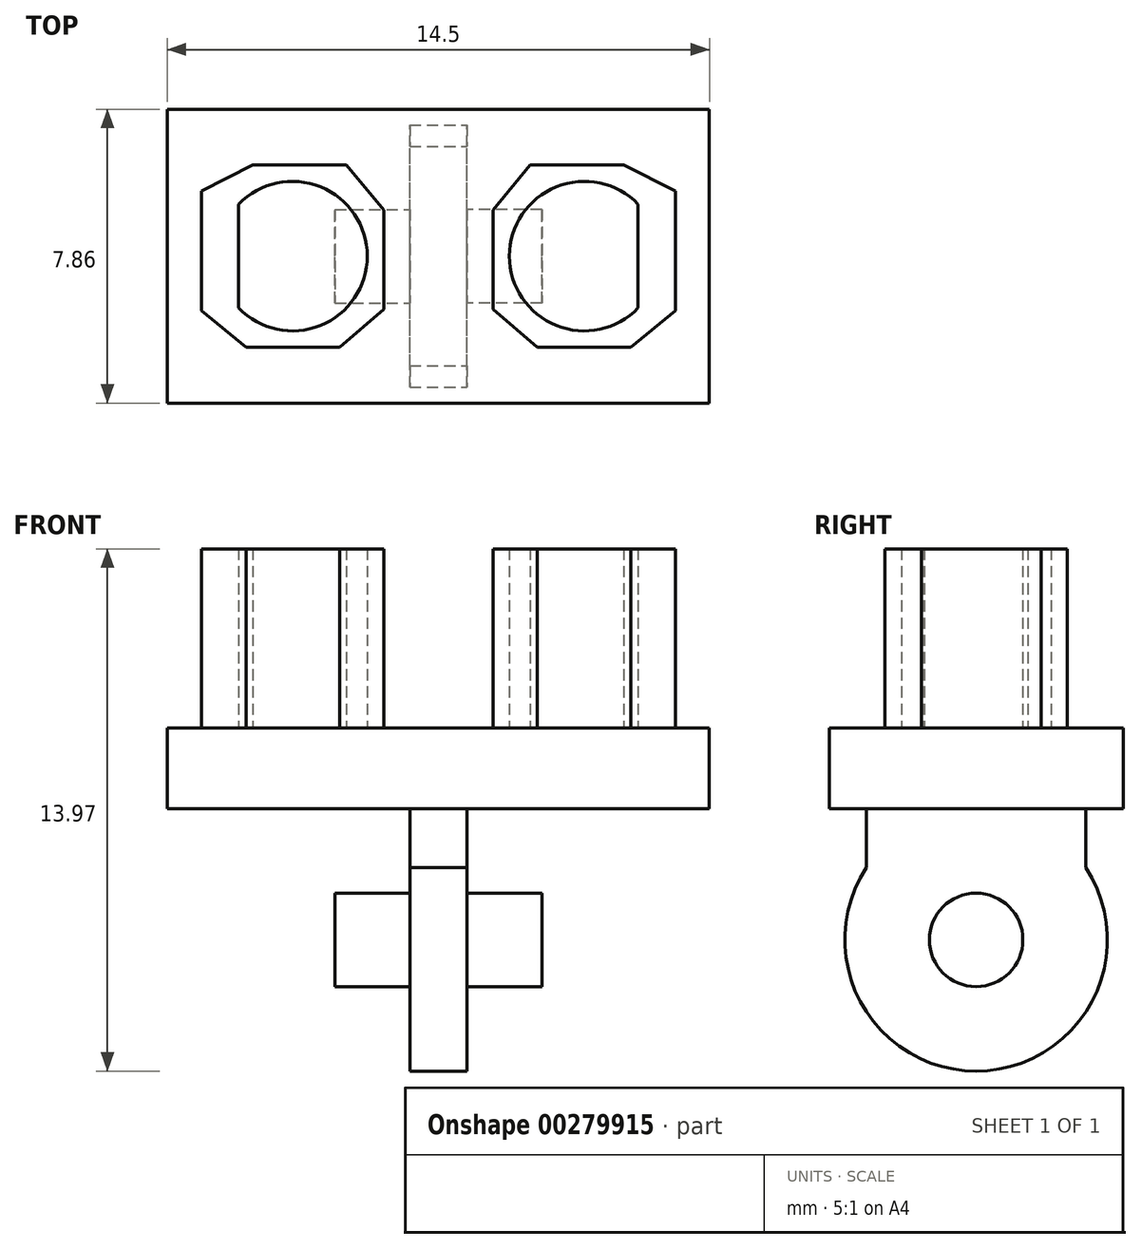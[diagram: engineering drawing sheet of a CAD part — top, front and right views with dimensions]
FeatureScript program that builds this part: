
annotation { "Feature Type Name" : "Feature", "Feature Type Description" : "" }
export const myFeature = defineFeature(function(context is Context, id is Id, definition is map)
    precondition{}
    {
        {
            var Q0;
            Q0=qCreatedBy(makeId("Top.planeOp"),FACE);
            var sketch = newSketch(context, id + "F0", { "sketchPlane" : qUnion([Q0])});
            skLineSegment(sketch, "E0.bottom", {"start": v(7.25, 3.93) * mm, "end": v(-7.25, 3.93) * mm});
            skLineSegment(sketch, "E0.top", {"start": v(7.25, -3.93) * mm, "end": v(-7.25, -3.93) * mm});
            skLineSegment(sketch, "E0.left", {"start": v(7.25, 3.93) * mm, "end": v(7.25, -3.93) * mm});
            skLineSegment(sketch, "E0.right", {"start": v(-7.25, 3.93) * mm, "end": v(-7.25, -3.93) * mm});
            skPoint(sketch, "E0.middle", {"position": v(0, 0) * mm});
            skSolve(sketch);
        }
        {
            var Q0;
            Q0=makeQuery(id+"F0.imprint","IMPRINT",FACE,{"disambiguationData":[TD([[makeQuery(id+"F0.imprint","IMPRINT",EDGE,{"derivedFrom":sQuery(id+"F0.wireOp",EDGE,"E0.bottom")}),1.0]])]});
            extrude(context, id + "F1", {"entities" : qUnion([Q0]), "oppositeDirection" : true, "depth" : 2.16 * mm});
        }
        {
            var Q0;
            Q0=makeQuery(id+"F1.opExtrude","CAP_FACE",FACE,{"disambiguationData":[OSD([sQuery(id+"F0.wireOp",EDGE,"E0.bottom"),sQuery(id+"F0.wireOp",EDGE,"E0.top"),sQuery(id+"F0.wireOp",EDGE,"E0.left"),sQuery(id+"F0.wireOp",EDGE,"E0.right")])],"isStart":false});
            var sketch = newSketch(context, id + "F2", { "sketchPlane" : qUnion([Q0])});
            skLineSegment(sketch, "E1.bottom", {"start": v(-0.77, 3.93) * mm, "end": v(0.77, 3.93) * mm});
            skLineSegment(sketch, "E1.top", {"start": v(-0.77, -3.93) * mm, "end": v(0.77, -3.93) * mm});
            skLineSegment(sketch, "E1.left", {"start": v(-0.77, 3.93) * mm, "end": v(-0.77, -3.93) * mm});
            skLineSegment(sketch, "E1.right", {"start": v(0.77, 3.93) * mm, "end": v(0.77, -3.93) * mm});
            skPoint(sketch, "E1.middle", {"position": v(0, 0) * mm});
            skSolve(sketch);
        }
        {
            var Q0;
            Q0=makeQuery(id+"F2.imprint","IMPRINT",FACE,{"disambiguationData":[TD([[makeQuery(id+"F2.imprint","IMPRINT",EDGE,{"derivedFrom":sQuery(id+"F2.wireOp",EDGE,"E1.bottom")}),1.0]])]});
            extrude(context, id + "F3", {"entities" : qUnion([Q0]), "operationType" : NewBodyOperationType.ADD, "depth" : 7.02 * mm});
        }
        {
            var Q0;
            Q0=makeQuery(id+"F3.opExtrude","SWEPT_FACE",FACE,{"disambiguationData":[OSD([sQuery(id+"F2.wireOp",EDGE,"E1.right")])]});
            var sketch = newSketch(context, id + "F4", { "sketchPlane" : qUnion([Q0])});
            skCircle(sketch, "E2", {"center": v(0, -5.67) * mm, "radius": 3.5 * mm});
            skLineSegment(sketch, "E3", {"start": v(-2.93, -2.16) * mm, "end": v(-2.93, -3.74) * mm});
            skLineSegment(sketch, "E4", {"start": v(2.93, -2.16) * mm, "end": v(2.93, -3.74) * mm});
            skCircle(sketch, "E5", {"center": v(0, -5.67) * mm, "radius": 1.25 * mm});
            skSolve(sketch);
        }
        {
            var Q0;
            {var subQ5=sQuery(id+"F4.wireOp",EDGE,"E3");Q0=makeQuery(id+"F4.imprint","IMPRINT",FACE,{"disambiguationData":[TD([[makeQuery(id+"F4.imprint","IMPRINT",EDGE,{"derivedFrom":subQ5}),-1.0]])]});}
            var Q1;
            {var subQ5=sQuery(id+"F4.wireOp",EDGE,"E4");Q1=makeQuery(id+"F4.imprint","IMPRINT",FACE,{"disambiguationData":[TD([[makeQuery(id+"F4.imprint","IMPRINT",EDGE,{"derivedFrom":subQ5}),1.0]])]});}
            extrude(context, id + "F5", {"entities" : qUnion([Q0, Q1]), "operationType" : NewBodyOperationType.REMOVE, "endBound" : BoundingType.THROUGH_ALL, "oppositeDirection" : true, "depth" : 25 * mm});
        }
        {
            var Q0;
            Q0=makeQuery(id+"F4.imprint","IMPRINT",FACE,{"disambiguationData":[TD([[makeQuery(id+"F4.imprint","IMPRINT",EDGE,{"derivedFrom":sQuery(id+"F4.wireOp",EDGE,"E5")}),1.0]])]});
            extrude(context, id + "F6", {"entities" : qUnion([Q0]), "operationType" : NewBodyOperationType.ADD, "depth" : 2 * mm});
        }
        {
            var Q0;
            Q0=makeQuery(id+"F1.opExtrude","SWEPT_BODY",BODY,{"disambiguationData":[OSD([sQuery(id+"F0.wireOp",EDGE,"E0.bottom"),sQuery(id+"F0.wireOp",EDGE,"E0.top"),sQuery(id+"F0.wireOp",EDGE,"E0.left"),sQuery(id+"F0.wireOp",EDGE,"E0.right")])]});
            var Q1;
            Q1=qCreatedBy(makeId("Right.planeOp"),FACE);
            mirror(context, id + "F7", {"operationType" : NewBodyOperationType.ADD, "entities" : qUnion([Q0]), "mirrorPlane" : qUnion([Q1])});
        }
        {
            var Q0;
            Q0=makeQuery(id+"F1.opExtrude","CAP_FACE",FACE,{"disambiguationData":[OSD([sQuery(id+"F0.wireOp",EDGE,"E0.bottom"),sQuery(id+"F0.wireOp",EDGE,"E0.top"),sQuery(id+"F0.wireOp",EDGE,"E0.left"),sQuery(id+"F0.wireOp",EDGE,"E0.right")])],"isStart":true});
            var sketch = newSketch(context, id + "F8", { "sketchPlane" : qUnion([Q0])});
            skLineSegment(sketch, "E6.bottom", {"start": v(1.46, 2.44) * mm, "end": v(6.34, 2.44) * mm});
            skLineSegment(sketch, "E6.top", {"start": v(1.46, -2.44) * mm, "end": v(6.34, -2.44) * mm});
            skLineSegment(sketch, "E6.left", {"start": v(1.46, 2.44) * mm, "end": v(1.46, -2.44) * mm});
            skLineSegment(sketch, "E6.right", {"start": v(6.34, 2.44) * mm, "end": v(6.34, -2.44) * mm});
            skPoint(sketch, "E6.middle", {"position": v(3.9, 0) * mm});
            skLineSegment(sketch, "E7", {"start": v(1.46, -1.42) * mm, "end": v(2.64, -2.44) * mm});
            skLineSegment(sketch, "E8", {"start": v(5.14, -2.44) * mm, "end": v(6.34, -1.46) * mm});
            skLineSegment(sketch, "E9", {"start": v(6.34, 1.74) * mm, "end": v(4.96, 2.44) * mm});
            skLineSegment(sketch, "E10", {"start": v(2.46, 2.44) * mm, "end": v(1.46, 1.24) * mm});
            skLineSegment(sketch, "E11", {"start": v(2.46, 2.44) * mm, "end": v(4.96, 2.44) * mm});
            skLineSegment(sketch, "E12", {"start": v(2.64, -2.44) * mm, "end": v(5.14, -2.44) * mm});
            skCircle(sketch, "E13", {"center": v(3.9, 0) * mm, "radius": 2 * mm});
            skLineSegment(sketch, "E14", {"start": v(5.34, 1.39) * mm, "end": v(5.34, -1.39) * mm});
            skSolve(sketch);
        }
        {
            var Q0;
            {var subQ3=sQuery(id+"F8.wireOp",EDGE,"E7");Q0=makeQuery(id+"F8.imprint","IMPRINT",FACE,{"disambiguationData":[TD([[makeQuery(id+"F8.imprint","IMPRINT",EDGE,{"derivedFrom":subQ3}),1.0]])]});}
            var Q1;
            {var subQ0=sQuery(id+"F8.wireOp",EDGE,"E14");Q1=makeQuery(id+"F8.imprint","IMPRINT",FACE,{"disambiguationData":[TD([[makeQuery(id+"F8.imprint","IMPRINT",EDGE,{"derivedFrom":subQ0}),1.0]])]});}
            extrude(context, id + "F9", {"entities" : qUnion([Q0, Q1]), "operationType" : NewBodyOperationType.ADD, "depth" : 4.8 * mm});
        }
        {
            var Q0;
            Q0=makeQuery(id+"F1.opExtrude","SWEPT_BODY",BODY,{"disambiguationData":[OSD([sQuery(id+"F0.wireOp",EDGE,"E0.bottom"),sQuery(id+"F0.wireOp",EDGE,"E0.top"),sQuery(id+"F0.wireOp",EDGE,"E0.left"),sQuery(id+"F0.wireOp",EDGE,"E0.right")])]});
            var Q1;
            Q1=qCreatedBy(makeId("Right.planeOp"),FACE);
            mirror(context, id + "F10", {"operationType" : NewBodyOperationType.ADD, "entities" : qUnion([Q0]), "mirrorPlane" : qUnion([Q1])});
        }
    });
